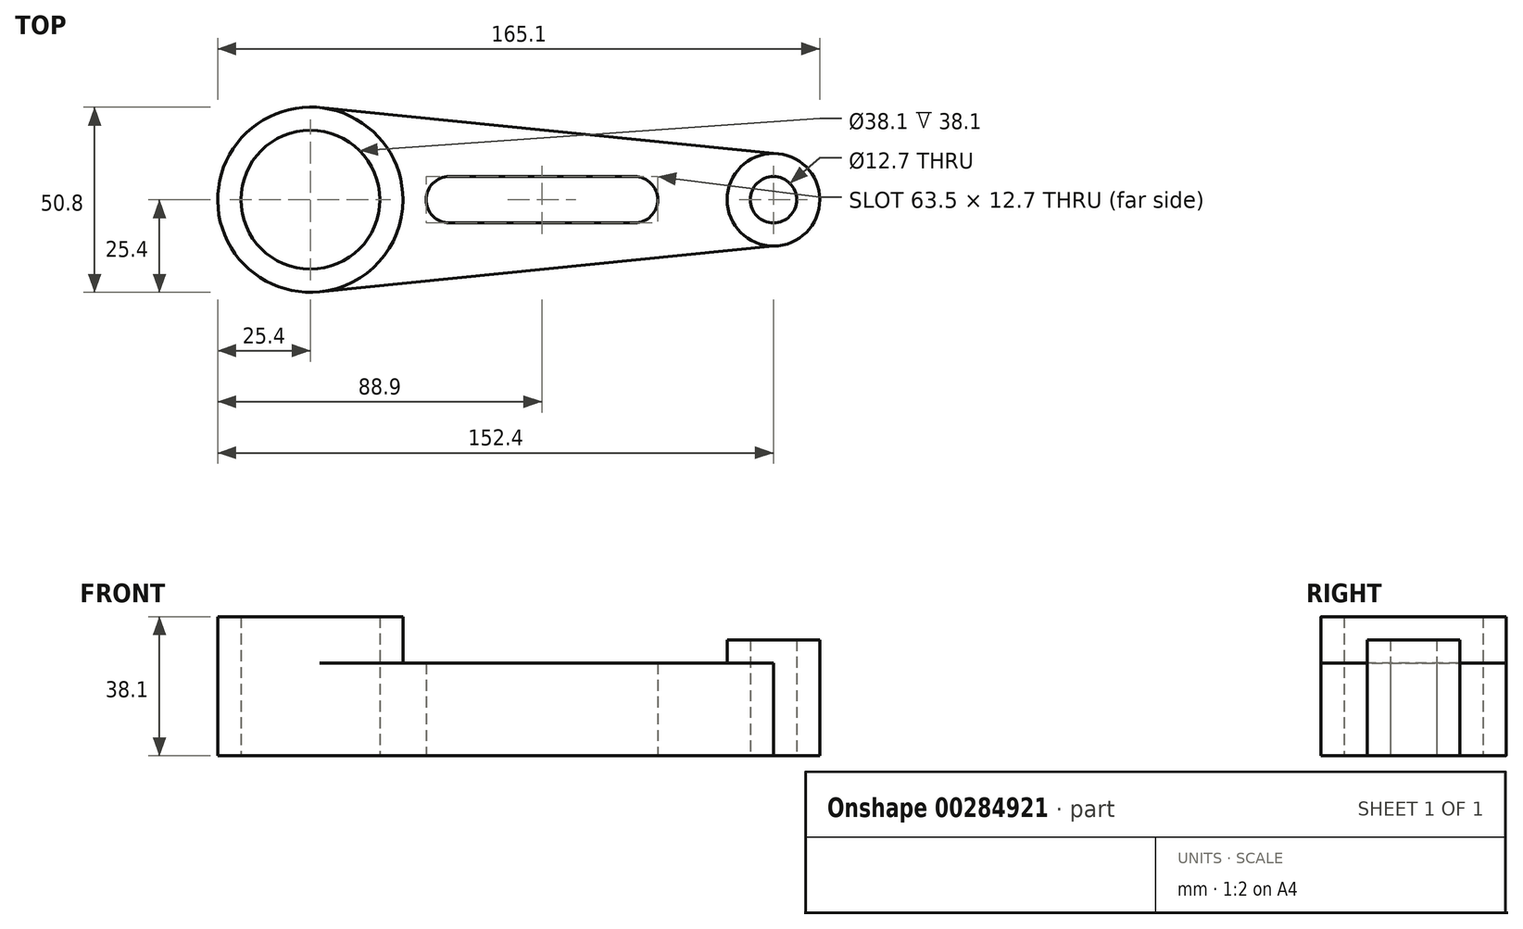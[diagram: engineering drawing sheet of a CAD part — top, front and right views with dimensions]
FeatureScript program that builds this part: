
annotation { "Feature Type Name" : "Feature", "Feature Type Description" : "" }
export const myFeature = defineFeature(function(context is Context, id is Id, definition is map)
    precondition{}
    {
        {
            var Q0;
            Q0=qCreatedBy(makeId("Top.planeOp"),FACE);
            var sketch = newSketch(context, id + "F0", { "sketchPlane" : qUnion([Q0])});
            skCircle(sketch, "E0", {"center": v(0, 0) * mm, "radius": 19.05 * mm});
            skCircle(sketch, "E1", {"center": v(0, 0) * mm, "radius": 25.4 * mm});
            skLineSegment(sketch, "E2", {"start": v(0, 0) * mm, "end": v(127, 0) * mm, "construction": true});
            skCircle(sketch, "E3", {"center": v(127, 0) * mm, "radius": 6.35 * mm});
            skCircle(sketch, "E4", {"center": v(127, 0) * mm, "radius": 12.7 * mm});
            skArc(sketch, "E5", {"start": v(88.9, -6.35) * mm, "mid": v(95.25, 0) * mm, "end": v(88.9, 6.35) * mm});
            skArc(sketch, "E6", {"start": v(38.1, 6.35) * mm, "mid": v(31.75, 0) * mm, "end": v(38.1, -6.35) * mm});
            skLineSegment(sketch, "E7", {"start": v(88.9, 0) * mm, "end": v(88.9, 6.35) * mm, "construction": true});
            skLineSegment(sketch, "E8", {"start": v(88.9, 6.35) * mm, "end": v(38.1, 6.35) * mm});
            skLineSegment(sketch, "E9", {"start": v(88.9, 0) * mm, "end": v(88.9, -6.35) * mm});
            skLineSegment(sketch, "E10", {"start": v(88.9, -6.35) * mm, "end": v(38.1, -6.35) * mm});
            skLineSegment(sketch, "E11", {"start": v(127, 12.7) * mm, "end": v(0, 25.53) * mm});
            skLineSegment(sketch, "E12", {"start": v(127, -12.7) * mm, "end": v(0, -25.53) * mm});
            skSolve(sketch);
        }
        {
            var Q0;
            Q0=makeQuery(id+"F0.imprint","IMPRINT",FACE,{"disambiguationData":[TD([[makeQuery(id+"F0.imprint","IMPRINT",EDGE,{"derivedFrom":sQuery(id+"F0.wireOp",EDGE,"E0")}),-1.0]])]});
            extrude(context, id + "F1", {"entities" : qUnion([Q0]), "depth" : 38.1 * mm});
        }
        {
            var Q0;
            Q0=makeQuery(id+"F0.imprint","IMPRINT",FACE,{"disambiguationData":[TD([[makeQuery(id+"F0.imprint","IMPRINT",EDGE,{"derivedFrom":sQuery(id+"F0.wireOp",EDGE,"E3")}),-1.0]])]});
            extrude(context, id + "F2", {"entities" : qUnion([Q0]), "depth" : 31.75 * mm});
        }
        {
            var Q0;
            Q0=makeQuery(id+"F0.imprint","IMPRINT",FACE,{"disambiguationData":[TD([[makeQuery(id+"F0.imprint","IMPRINT",EDGE,{"derivedFrom":sQuery(id+"F0.wireOp",EDGE,"E5")}),-1.0]])]});
            extrude(context, id + "F3", {"entities" : qUnion([Q0]), "operationType" : NewBodyOperationType.ADD, "depth" : 25.4 * mm});
        }
    });
